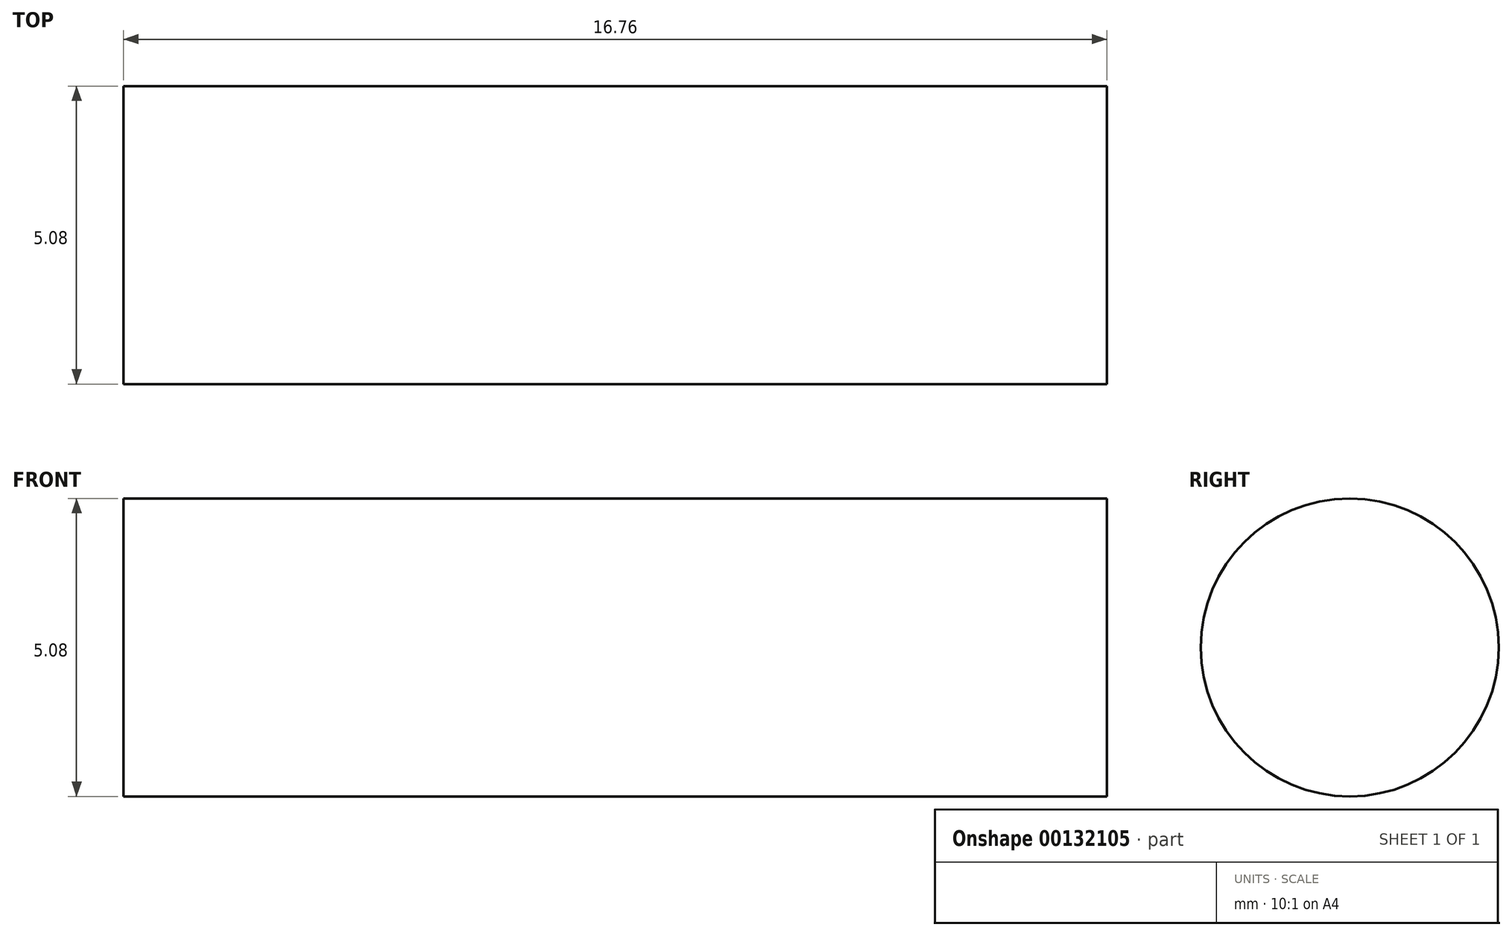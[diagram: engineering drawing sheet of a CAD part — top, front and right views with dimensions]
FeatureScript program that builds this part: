
annotation { "Feature Type Name" : "Feature", "Feature Type Description" : "" }
export const myFeature = defineFeature(function(context is Context, id is Id, definition is map)
    precondition{}
    {
        {
            var Q0;
            Q0=qCreatedBy(makeId("Right.planeOp"),FACE);
            var sketch = newSketch(context, id + "F0", { "sketchPlane" : qUnion([Q0])});
            skCircle(sketch, "E0", {"center": v(0, 0) * mm, "radius": 12.7 * mm});
            skSolve(sketch);
        }
        {
            var Q0;
            Q0 = qSketchRegion(id + "F0", true);
            var Q1;
            Q1=makeQuery(id+"F0.imprint","IMPRINT",FACE,{"disambiguationData":[TD([[makeQuery(id+"F0.imprint","IMPRINT",EDGE,{"derivedFrom":sQuery(id+"F0.wireOp",EDGE,"E0")}),1.0]])]});
            extrude(context, id + "F1", {"entities" : qUnion([Q0, Q1]), "depth" : 83.82 * mm});
        }
        {
            var Q0;
            Q0=makeQuery(id+"F1.opExtrude","SWEPT_BODY",BODY,{"disambiguationData":[OSD([sQuery(id+"F0.wireOp",EDGE,"E0")])]});
            var Q1;
            Q1=qCreatedBy(makeId("Origin.pointOp"),VERTEX);
            transform(context, id + "F2", {"entities" : qUnion([Q0]), "transformType" : TransformType.SCALE_UNIFORMLY, "scale" : .2, "scalePoint" : qUnion([Q1]), "makeCopy" : false});
        }
    });
